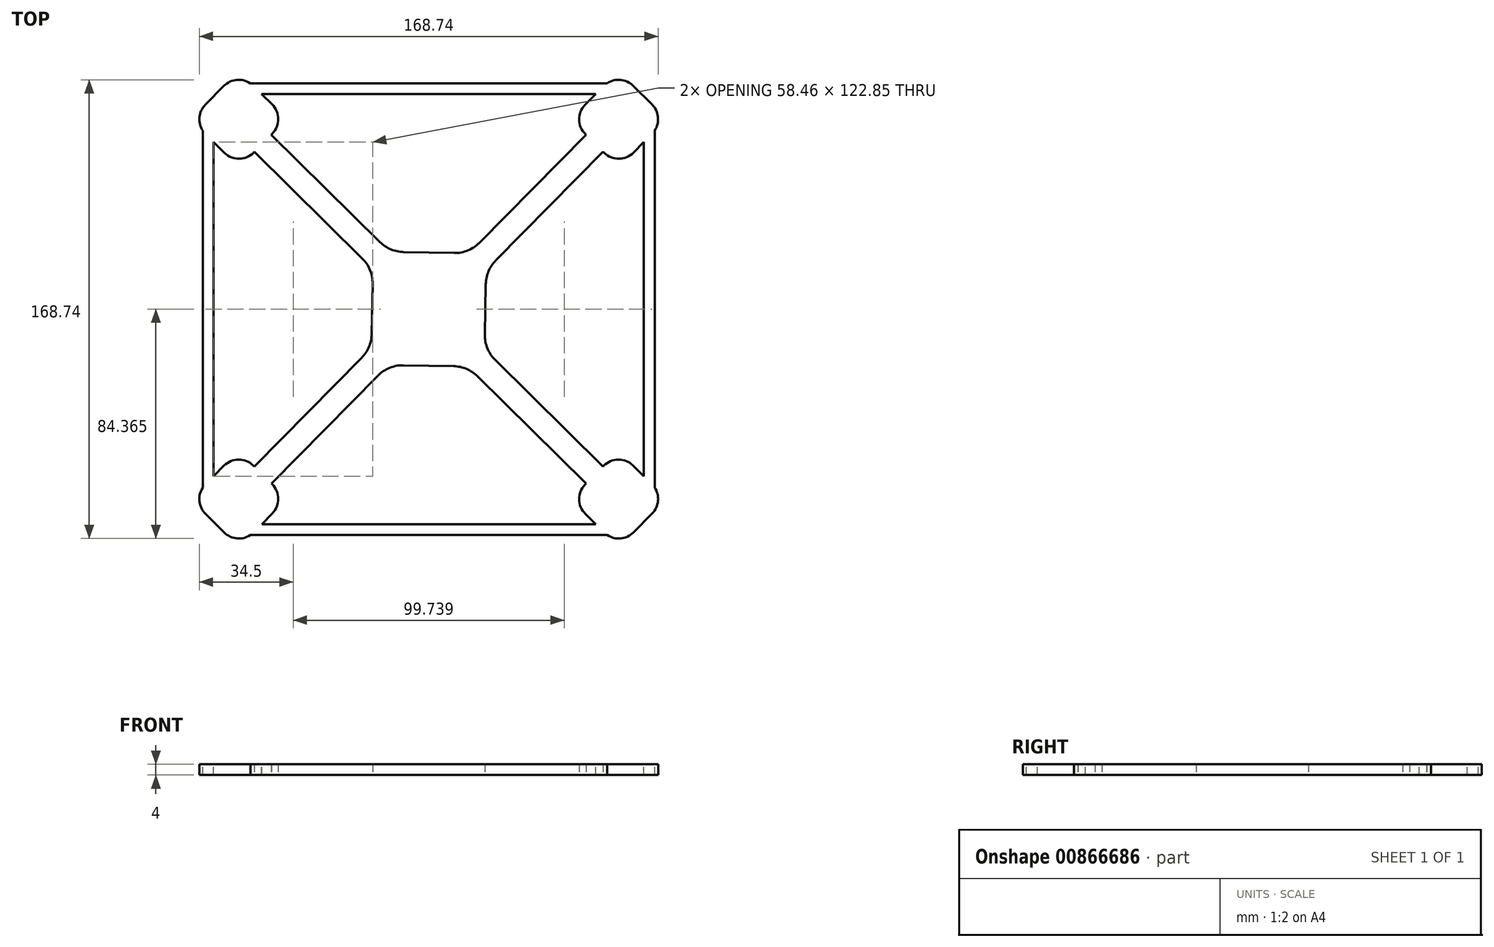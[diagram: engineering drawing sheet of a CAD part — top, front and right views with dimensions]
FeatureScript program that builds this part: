
annotation { "Feature Type Name" : "Feature", "Feature Type Description" : "" }
export const myFeature = defineFeature(function(context is Context, id is Id, definition is map)
    precondition{}
    {
        {
            var Q0;
            Q0=qCreatedBy(makeId("Top.planeOp"),FACE);
            var sketch = newSketch(context, id + "F0", { "sketchPlane" : qUnion([Q0])});
            skCircle(sketch, "E0", {"center": v(-69.85, -69.85) * mm, "radius": 63.5 * mm});
            skCircle(sketch, "E1", {"center": v(69.85, -69.85) * mm, "radius": 63.5 * mm});
            skCircle(sketch, "E2", {"center": v(69.85, 69.85) * mm, "radius": 63.5 * mm});
            skCircle(sketch, "E3", {"center": v(-69.85, 69.85) * mm, "radius": 63.5 * mm});
            skLineSegment(sketch, "E4.0", {"start": v(24.66, 17.89) * mm, "end": v(64.17, 57.89) * mm});
            skLineSegment(sketch, "E5.0", {"start": v(18.6, 24.41) * mm, "end": v(57.85, 64.14) * mm});
            skLineSegment(sketch, "E6", {"start": v(78.63, 78.74) * mm, "end": v(82.1, 75.31) * mm});
            skLineSegment(sketch, "E7", {"start": v(78.63, 78.74) * mm, "end": v(75.16, 82.17) * mm});
            skLineSegment(sketch, "E8", {"start": v(64.39, 82.1) * mm, "end": v(57.53, 75.16) * mm});
            skLineSegment(sketch, "E9", {"start": v(78.74, 61.07) * mm, "end": v(82.17, 64.54) * mm});
            skLineSegment(sketch, "E10", {"start": v(64.17, 57.89) * mm, "end": v(64.54, 57.53) * mm});
            skLineSegment(sketch, "E11", {"start": v(75.31, 57.6) * mm, "end": v(78.74, 61.07) * mm});
            skLineSegment(sketch, "E12", {"start": v(57.6, 64.39) * mm, "end": v(57.85, 64.14) * mm});
            skPoint(sketch, "E13.visualSharp", {"position": v(52.17, 69.74) * mm});
            skPoint(sketch, "E14.visualSharp", {"position": v(69.74, 87.53) * mm});
            skArc(sketch, "E14.filletArc", {"start": v(75.16, 82.17) * mm, "mid": v(69.76, 84.37) * mm, "end": v(64.39, 82.1) * mm});
            skArc(sketch, "E15.filletArc", {"start": v(57.53, 75.16) * mm, "mid": v(55.33, 69.76) * mm, "end": v(57.6, 64.39) * mm});
            skPoint(sketch, "E16.visualSharp", {"position": v(69.96, 52.17) * mm});
            skArc(sketch, "E16.filletArc", {"start": v(64.54, 57.53) * mm, "mid": v(69.94, 55.33) * mm, "end": v(75.31, 57.6) * mm});
            skPoint(sketch, "E17.visualSharp", {"position": v(11.4, 17.11) * mm});
            skLineSegment(sketch, "E18", {"start": v(0, 0) * mm, "end": v(69.85, 69.85) * mm});
            skLineSegment(sketch, "E19", {"start": v(57.85, 64.14) * mm, "end": v(61, 61) * mm});
            skLineSegment(sketch, "E20", {"start": v(61, 61) * mm, "end": v(64.17, 57.89) * mm});
            skPoint(sketch, "E21.1.0", {"position": v(-87.53, 69.74) * mm});
            skLineSegment(sketch, "E21.1.1", {"start": v(-61.07, 78.74) * mm, "end": v(-64.54, 82.17) * mm});
            skPoint(sketch, "E21.1.2", {"position": v(-69.74, 52.17) * mm});
            skPoint(sketch, "E21.1.3", {"position": v(-52.17, 69.96) * mm});
            skLineSegment(sketch, "E21.1.4", {"start": v(-17.89, 24.66) * mm, "end": v(-57.89, 64.17) * mm});
            skLineSegment(sketch, "E21.1.5", {"start": v(-24.41, 18.6) * mm, "end": v(-64.14, 57.85) * mm});
            skLineSegment(sketch, "E21.1.6", {"start": v(0, 0) * mm, "end": v(-69.85, 69.85) * mm});
            skLineSegment(sketch, "E21.1.7", {"start": v(-82.1, 64.39) * mm, "end": v(-75.16, 57.53) * mm});
            skArc(sketch, "E21.1.8", {"start": v(-82.17, 75.16) * mm, "mid": v(-84.37, 69.76) * mm, "end": v(-82.1, 64.39) * mm});
            skPoint(sketch, "E21.1.9", {"position": v(-69.74, 52.17) * mm});
            skArc(sketch, "E21.1.10", {"start": v(-57.53, 64.54) * mm, "mid": v(-55.33, 69.94) * mm, "end": v(-57.6, 75.31) * mm});
            skLineSegment(sketch, "E21.1.11", {"start": v(-78.74, 78.63) * mm, "end": v(-75.31, 82.1) * mm});
            skLineSegment(sketch, "E21.1.12", {"start": v(-78.74, 78.63) * mm, "end": v(-82.17, 75.16) * mm});
            skLineSegment(sketch, "E21.1.13", {"start": v(-57.6, 75.31) * mm, "end": v(-61.07, 78.74) * mm});
            skArc(sketch, "E21.1.14", {"start": v(-75.16, 57.53) * mm, "mid": v(-69.76, 55.33) * mm, "end": v(-64.39, 57.6) * mm});
            skLineSegment(sketch, "E21.1.15", {"start": v(-61, 61) * mm, "end": v(-57.89, 64.17) * mm});
            skLineSegment(sketch, "E21.1.16", {"start": v(-64.14, 57.85) * mm, "end": v(-61, 61) * mm});
            skLineSegment(sketch, "E21.1.17", {"start": v(-57.89, 64.17) * mm, "end": v(-57.53, 64.54) * mm});
            skLineSegment(sketch, "E21.1.18", {"start": v(-64.39, 57.6) * mm, "end": v(-64.14, 57.85) * mm});
            skPoint(sketch, "E21.2.0", {"position": v(-69.74, -87.53) * mm});
            skLineSegment(sketch, "E21.2.1", {"start": v(-78.74, -61.07) * mm, "end": v(-82.17, -64.54) * mm});
            skPoint(sketch, "E21.2.2", {"position": v(-52.17, -69.74) * mm});
            skPoint(sketch, "E21.2.3", {"position": v(-69.96, -52.17) * mm});
            skLineSegment(sketch, "E21.2.4", {"start": v(-24.66, -17.89) * mm, "end": v(-64.17, -57.89) * mm});
            skLineSegment(sketch, "E21.2.5", {"start": v(-18.6, -24.41) * mm, "end": v(-57.85, -64.14) * mm});
            skLineSegment(sketch, "E21.2.6", {"start": v(0, 0) * mm, "end": v(-69.85, -69.85) * mm});
            skLineSegment(sketch, "E21.2.7", {"start": v(-64.39, -82.1) * mm, "end": v(-57.53, -75.16) * mm});
            skArc(sketch, "E21.2.8", {"start": v(-75.16, -82.17) * mm, "mid": v(-69.76, -84.37) * mm, "end": v(-64.39, -82.1) * mm});
            skPoint(sketch, "E21.2.9", {"position": v(-52.17, -69.74) * mm});
            skArc(sketch, "E21.2.10", {"start": v(-64.54, -57.53) * mm, "mid": v(-69.94, -55.33) * mm, "end": v(-75.31, -57.6) * mm});
            skLineSegment(sketch, "E21.2.11", {"start": v(-78.63, -78.74) * mm, "end": v(-82.1, -75.31) * mm});
            skLineSegment(sketch, "E21.2.12", {"start": v(-78.63, -78.74) * mm, "end": v(-75.16, -82.17) * mm});
            skLineSegment(sketch, "E21.2.13", {"start": v(-75.31, -57.6) * mm, "end": v(-78.74, -61.07) * mm});
            skArc(sketch, "E21.2.14", {"start": v(-57.53, -75.16) * mm, "mid": v(-55.33, -69.76) * mm, "end": v(-57.6, -64.39) * mm});
            skLineSegment(sketch, "E21.2.15", {"start": v(-61, -61) * mm, "end": v(-64.17, -57.89) * mm});
            skLineSegment(sketch, "E21.2.16", {"start": v(-57.85, -64.14) * mm, "end": v(-61, -61) * mm});
            skLineSegment(sketch, "E21.2.17", {"start": v(-64.17, -57.89) * mm, "end": v(-64.54, -57.53) * mm});
            skLineSegment(sketch, "E21.2.18", {"start": v(-57.6, -64.39) * mm, "end": v(-57.85, -64.14) * mm});
            skPoint(sketch, "E21.3.0", {"position": v(87.53, -69.74) * mm});
            skLineSegment(sketch, "E21.3.1", {"start": v(61.07, -78.74) * mm, "end": v(64.54, -82.17) * mm});
            skPoint(sketch, "E21.3.2", {"position": v(69.74, -52.17) * mm});
            skPoint(sketch, "E21.3.3", {"position": v(52.17, -69.96) * mm});
            skLineSegment(sketch, "E21.3.4", {"start": v(17.89, -24.66) * mm, "end": v(57.89, -64.17) * mm});
            skLineSegment(sketch, "E21.3.5", {"start": v(24.41, -18.6) * mm, "end": v(64.14, -57.85) * mm});
            skLineSegment(sketch, "E21.3.6", {"start": v(0, 0) * mm, "end": v(69.85, -69.85) * mm});
            skLineSegment(sketch, "E21.3.7", {"start": v(82.1, -64.39) * mm, "end": v(75.16, -57.53) * mm});
            skArc(sketch, "E21.3.8", {"start": v(82.17, -75.16) * mm, "mid": v(84.37, -69.76) * mm, "end": v(82.1, -64.39) * mm});
            skPoint(sketch, "E21.3.9", {"position": v(69.74, -52.17) * mm});
            skArc(sketch, "E21.3.10", {"start": v(57.53, -64.54) * mm, "mid": v(55.33, -69.94) * mm, "end": v(57.6, -75.31) * mm});
            skLineSegment(sketch, "E21.3.11", {"start": v(78.74, -78.63) * mm, "end": v(75.31, -82.1) * mm});
            skLineSegment(sketch, "E21.3.12", {"start": v(78.74, -78.63) * mm, "end": v(82.17, -75.16) * mm});
            skLineSegment(sketch, "E21.3.13", {"start": v(57.6, -75.31) * mm, "end": v(61.07, -78.74) * mm});
            skArc(sketch, "E21.3.14", {"start": v(75.16, -57.53) * mm, "mid": v(69.76, -55.33) * mm, "end": v(64.39, -57.6) * mm});
            skLineSegment(sketch, "E21.3.15", {"start": v(61, -61) * mm, "end": v(57.89, -64.17) * mm});
            skLineSegment(sketch, "E21.3.16", {"start": v(64.14, -57.85) * mm, "end": v(61, -61) * mm});
            skLineSegment(sketch, "E21.3.17", {"start": v(57.89, -64.17) * mm, "end": v(57.53, -64.54) * mm});
            skLineSegment(sketch, "E21.3.18", {"start": v(64.39, -57.6) * mm, "end": v(64.14, -57.85) * mm});
            skPoint(sketch, "E21.center", {"position": v(0, 0) * mm});
            skLineSegment(sketch, "E22", {"start": v(21, 9.2) * mm, "end": v(20.64, -9.33) * mm});
            skLineSegment(sketch, "E23", {"start": v(9.2, -21) * mm, "end": v(-9.33, -20.64) * mm});
            skLineSegment(sketch, "E24", {"start": v(-21, -9.2) * mm, "end": v(-20.64, 9.33) * mm});
            skLineSegment(sketch, "E25", {"start": v(-9.2, 21) * mm, "end": v(9.33, 20.64) * mm});
            skPoint(sketch, "E26.visualSharp", {"position": v(69.96, -87.53) * mm});
            skArc(sketch, "E26.filletArc", {"start": v(64.54, -82.17) * mm, "mid": v(69.94, -84.37) * mm, "end": v(75.31, -82.1) * mm});
            skPoint(sketch, "E27.visualSharp", {"position": v(-87.53, -69.96) * mm});
            skArc(sketch, "E27.filletArc", {"start": v(-82.17, -64.54) * mm, "mid": v(-84.37, -69.94) * mm, "end": v(-82.1, -75.31) * mm});
            skPoint(sketch, "E28.visualSharp", {"position": v(-69.96, 87.53) * mm});
            skArc(sketch, "E28.filletArc", {"start": v(-64.54, 82.17) * mm, "mid": v(-69.94, 84.37) * mm, "end": v(-75.31, 82.1) * mm});
            skPoint(sketch, "E29.visualSharp", {"position": v(87.53, 69.96) * mm});
            skArc(sketch, "E29.filletArc", {"start": v(82.17, 64.54) * mm, "mid": v(84.37, 69.94) * mm, "end": v(82.1, 75.31) * mm});
            skPoint(sketch, "E30.visualSharp", {"position": v(-14.28, 21.1) * mm});
            skArc(sketch, "E30.filletArc", {"start": v(-17.89, 24.66) * mm, "mid": v(-13.9, 21.99) * mm, "end": v(-9.2, 21) * mm});
            skPoint(sketch, "E31.visualSharp", {"position": v(-20.53, 14.77) * mm});
            skArc(sketch, "E31.filletArc", {"start": v(-20.64, 9.33) * mm, "mid": v(-21.57, 14.35) * mm, "end": v(-24.41, 18.6) * mm});
            skPoint(sketch, "E32.visualSharp", {"position": v(-21.1, -14.28) * mm});
            skArc(sketch, "E32.filletArc", {"start": v(-24.66, -17.89) * mm, "mid": v(-21.99, -13.9) * mm, "end": v(-21, -9.2) * mm});
            skPoint(sketch, "E33.visualSharp", {"position": v(-14.77, -20.53) * mm});
            skArc(sketch, "E33.filletArc", {"start": v(-9.33, -20.64) * mm, "mid": v(-14.35, -21.57) * mm, "end": v(-18.6, -24.41) * mm});
            skPoint(sketch, "E34.visualSharp", {"position": v(14.28, -21.1) * mm});
            skArc(sketch, "E34.filletArc", {"start": v(17.89, -24.66) * mm, "mid": v(13.9, -21.99) * mm, "end": v(9.2, -21) * mm});
            skPoint(sketch, "E35.visualSharp", {"position": v(20.53, -14.77) * mm});
            skArc(sketch, "E35.filletArc", {"start": v(20.64, -9.33) * mm, "mid": v(21.57, -14.35) * mm, "end": v(24.41, -18.6) * mm});
            skPoint(sketch, "E36.visualSharp", {"position": v(21.1, 14.28) * mm});
            skArc(sketch, "E36.filletArc", {"start": v(24.66, 17.89) * mm, "mid": v(21.99, 13.9) * mm, "end": v(21, 9.2) * mm});
            skPoint(sketch, "E37.visualSharp", {"position": v(14.77, 20.53) * mm});
            skArc(sketch, "E37.filletArc", {"start": v(9.33, 20.64) * mm, "mid": v(14.35, 21.57) * mm, "end": v(18.6, 24.41) * mm});
            skSolve(sketch);
        }
        {
            var Q0;
            Q0=makeQuery(id+"F0.imprint","IMPRINT",FACE,{"disambiguationData":[TD([[makeQuery(id+"F0.imprint","IMPRINT",EDGE,{"derivedFrom":sQuery(id+"F0.wireOp",EDGE,"E21.1.1")}),1.0]])]});
            var Q1;
            {var subQ5=sQuery(id+"F0.wireOp",EDGE,"E21.1.15");Q1=makeQuery(id+"F0.imprint","IMPRINT",FACE,{"disambiguationData":[TD([[makeQuery(id+"F0.imprint","IMPRINT",EDGE,{"derivedFrom":subQ5}),-1.0]])]});}
            var Q2;
            {var subQ5=sQuery(id+"F0.wireOp",EDGE,"E21.1.16");Q2=makeQuery(id+"F0.imprint","IMPRINT",FACE,{"disambiguationData":[TD([[makeQuery(id+"F0.imprint","IMPRINT",EDGE,{"derivedFrom":subQ5}),-1.0]])]});}
            var Q3;
            Q3=makeQuery(id+"F0.imprint","IMPRINT",FACE,{"disambiguationData":[TD([[makeQuery(id+"F0.imprint","IMPRINT",EDGE,{"derivedFrom":sQuery(id+"F0.wireOp",EDGE,"E25")}),-1.0]])]});
            var Q4;
            Q4=makeQuery(id+"F0.imprint","IMPRINT",FACE,{"disambiguationData":[TD([[makeQuery(id+"F0.imprint","IMPRINT",EDGE,{"derivedFrom":sQuery(id+"F0.wireOp",EDGE,"E24")}),-1.0]])]});
            var Q5;
            Q5=makeQuery(id+"F0.imprint","IMPRINT",FACE,{"disambiguationData":[TD([[makeQuery(id+"F0.imprint","IMPRINT",EDGE,{"derivedFrom":sQuery(id+"F0.wireOp",EDGE,"E23")}),-1.0]])]});
            var Q6;
            Q6=makeQuery(id+"F0.imprint","IMPRINT",FACE,{"disambiguationData":[TD([[makeQuery(id+"F0.imprint","IMPRINT",EDGE,{"derivedFrom":sQuery(id+"F0.wireOp",EDGE,"E22")}),-1.0]])]});
            var Q7;
            {var subQ5=sQuery(id+"F0.wireOp",EDGE,"E20");Q7=makeQuery(id+"F0.imprint","IMPRINT",FACE,{"disambiguationData":[TD([[makeQuery(id+"F0.imprint","IMPRINT",EDGE,{"derivedFrom":subQ5}),-1.0]])]});}
            var Q8;
            {var subQ5=sQuery(id+"F0.wireOp",EDGE,"E19");Q8=makeQuery(id+"F0.imprint","IMPRINT",FACE,{"disambiguationData":[TD([[makeQuery(id+"F0.imprint","IMPRINT",EDGE,{"derivedFrom":subQ5}),-1.0]])]});}
            var Q9;
            Q9=makeQuery(id+"F0.imprint","IMPRINT",FACE,{"disambiguationData":[TD([[makeQuery(id+"F0.imprint","IMPRINT",EDGE,{"derivedFrom":sQuery(id+"F0.wireOp",EDGE,"E6")}),-1.0]])]});
            var Q10;
            Q10=makeQuery(id+"F0.imprint","IMPRINT",FACE,{"disambiguationData":[TD([[makeQuery(id+"F0.imprint","IMPRINT",EDGE,{"derivedFrom":sQuery(id+"F0.wireOp",EDGE,"E21.3.1")}),1.0]])]});
            var Q11;
            {var subQ5=sQuery(id+"F0.wireOp",EDGE,"E21.3.16");Q11=makeQuery(id+"F0.imprint","IMPRINT",FACE,{"disambiguationData":[TD([[makeQuery(id+"F0.imprint","IMPRINT",EDGE,{"derivedFrom":subQ5}),-1.0]])]});}
            var Q12;
            {var subQ5=sQuery(id+"F0.wireOp",EDGE,"E21.3.15");Q12=makeQuery(id+"F0.imprint","IMPRINT",FACE,{"disambiguationData":[TD([[makeQuery(id+"F0.imprint","IMPRINT",EDGE,{"derivedFrom":subQ5}),-1.0]])]});}
            var Q13;
            {var subQ5=sQuery(id+"F0.wireOp",EDGE,"E21.2.16");Q13=makeQuery(id+"F0.imprint","IMPRINT",FACE,{"disambiguationData":[TD([[makeQuery(id+"F0.imprint","IMPRINT",EDGE,{"derivedFrom":subQ5}),-1.0]])]});}
            var Q14;
            {var subQ5=sQuery(id+"F0.wireOp",EDGE,"E21.2.15");Q14=makeQuery(id+"F0.imprint","IMPRINT",FACE,{"disambiguationData":[TD([[makeQuery(id+"F0.imprint","IMPRINT",EDGE,{"derivedFrom":subQ5}),-1.0]])]});}
            var Q15;
            Q15=makeQuery(id+"F0.imprint","IMPRINT",FACE,{"disambiguationData":[TD([[makeQuery(id+"F0.imprint","IMPRINT",EDGE,{"derivedFrom":sQuery(id+"F0.wireOp",EDGE,"E21.2.1")}),1.0]])]});
            extrude(context, id + "F1", {"entities" : qUnion([Q0, Q1, Q2, Q3, Q4, Q5, Q6, Q7, Q8, Q9, Q10, Q11, Q12, Q13, Q14, Q15]), "depth" : 4 * mm, "offsetDistance" : 25.4 * mm});
        }
        {
            var Q0;
            Q0=makeQuery(id+"F1.opExtrude","CAP_FACE",FACE,{"disambiguationData":[OSD([sQuery(id+"F0.wireOp",EDGE,"E4.0"),sQuery(id+"F0.wireOp",EDGE,"E5.0"),sQuery(id+"F0.wireOp",EDGE,"E6"),sQuery(id+"F0.wireOp",EDGE,"E7"),sQuery(id+"F0.wireOp",EDGE,"E8"),sQuery(id+"F0.wireOp",EDGE,"E9"),sQuery(id+"F0.wireOp",EDGE,"E10"),sQuery(id+"F0.wireOp",EDGE,"E11"),sQuery(id+"F0.wireOp",EDGE,"E12"),sQuery(id+"F0.wireOp",EDGE,"E14.filletArc"),sQuery(id+"F0.wireOp",EDGE,"E15.filletArc"),sQuery(id+"F0.wireOp",EDGE,"E16.filletArc"),sQuery(id+"F0.wireOp",EDGE,"E21.1.1"),sQuery(id+"F0.wireOp",EDGE,"E21.1.4"),sQuery(id+"F0.wireOp",EDGE,"E21.1.5"),sQuery(id+"F0.wireOp",EDGE,"E21.1.7"),sQuery(id+"F0.wireOp",EDGE,"E21.1.8"),sQuery(id+"F0.wireOp",EDGE,"E21.1.10"),sQuery(id+"F0.wireOp",EDGE,"E21.1.11"),sQuery(id+"F0.wireOp",EDGE,"E21.1.12"),sQuery(id+"F0.wireOp",EDGE,"E21.1.13"),sQuery(id+"F0.wireOp",EDGE,"E21.1.14"),sQuery(id+"F0.wireOp",EDGE,"E21.1.17"),sQuery(id+"F0.wireOp",EDGE,"E21.1.18"),sQuery(id+"F0.wireOp",EDGE,"E21.2.1"),sQuery(id+"F0.wireOp",EDGE,"E21.2.4"),sQuery(id+"F0.wireOp",EDGE,"E21.2.5"),sQuery(id+"F0.wireOp",EDGE,"E21.2.7"),sQuery(id+"F0.wireOp",EDGE,"E21.2.8"),sQuery(id+"F0.wireOp",EDGE,"E21.2.10"),sQuery(id+"F0.wireOp",EDGE,"E21.2.11"),sQuery(id+"F0.wireOp",EDGE,"E21.2.12"),sQuery(id+"F0.wireOp",EDGE,"E21.2.13"),sQuery(id+"F0.wireOp",EDGE,"E21.2.14"),sQuery(id+"F0.wireOp",EDGE,"E21.2.17"),sQuery(id+"F0.wireOp",EDGE,"E21.2.18"),sQuery(id+"F0.wireOp",EDGE,"E21.3.1"),sQuery(id+"F0.wireOp",EDGE,"E21.3.4"),sQuery(id+"F0.wireOp",EDGE,"E21.3.5"),sQuery(id+"F0.wireOp",EDGE,"E21.3.7"),sQuery(id+"F0.wireOp",EDGE,"E21.3.8"),sQuery(id+"F0.wireOp",EDGE,"E21.3.10"),sQuery(id+"F0.wireOp",EDGE,"E21.3.11"),sQuery(id+"F0.wireOp",EDGE,"E21.3.12"),sQuery(id+"F0.wireOp",EDGE,"E21.3.13"),sQuery(id+"F0.wireOp",EDGE,"E21.3.14"),sQuery(id+"F0.wireOp",EDGE,"E21.3.17"),sQuery(id+"F0.wireOp",EDGE,"E21.3.18"),sQuery(id+"F0.wireOp",EDGE,"E22"),sQuery(id+"F0.wireOp",EDGE,"E23"),sQuery(id+"F0.wireOp",EDGE,"E24"),sQuery(id+"F0.wireOp",EDGE,"E25"),sQuery(id+"F0.wireOp",EDGE,"E26.filletArc"),sQuery(id+"F0.wireOp",EDGE,"E27.filletArc"),sQuery(id+"F0.wireOp",EDGE,"E28.filletArc"),sQuery(id+"F0.wireOp",EDGE,"E29.filletArc"),sQuery(id+"F0.wireOp",EDGE,"E30.filletArc"),sQuery(id+"F0.wireOp",EDGE,"E31.filletArc"),sQuery(id+"F0.wireOp",EDGE,"E32.filletArc"),sQuery(id+"F0.wireOp",EDGE,"E33.filletArc"),sQuery(id+"F0.wireOp",EDGE,"E34.filletArc"),sQuery(id+"F0.wireOp",EDGE,"E35.filletArc"),sQuery(id+"F0.wireOp",EDGE,"E36.filletArc"),sQuery(id+"F0.wireOp",EDGE,"E37.filletArc")])],"isStart":false});
            var sketch = newSketch(context, id + "F2", { "sketchPlane" : qUnion([Q0])});
            skLineSegment(sketch, "E38", {"start": v(-69.85, -83.1) * mm, "end": v(69.85, -83.1) * mm});
            skPoint(sketch, "E38.startSnap0", {"position": v(-69.77, -83.1) * mm});
            skLineSegment(sketch, "E39.0", {"start": v(-63.2, -79.1) * mm, "end": v(63.24, -79.1) * mm});
            skLineSegment(sketch, "E40.1.0", {"start": v(83.1, -69.85) * mm, "end": v(83.1, 69.85) * mm});
            skLineSegment(sketch, "E40.1.1", {"start": v(79.1, -63.2) * mm, "end": v(79.1, 63.24) * mm});
            skLineSegment(sketch, "E40.2.0", {"start": v(69.85, 83.1) * mm, "end": v(-69.85, 83.1) * mm});
            skLineSegment(sketch, "E40.2.1", {"start": v(63.2, 79.1) * mm, "end": v(-63.24, 79.1) * mm});
            skLineSegment(sketch, "E40.3.0", {"start": v(-83.1, 69.85) * mm, "end": v(-83.1, -69.85) * mm});
            skLineSegment(sketch, "E40.3.1", {"start": v(-79.1, 63.2) * mm, "end": v(-79.1, -63.24) * mm});
            skPoint(sketch, "E40.center", {"position": v(0, 0) * mm});
            skSolve(sketch);
        }
        {
            var Q0;
            {var subQ11=sQuery(id+"F2.wireOp",EDGE,"E40.2.1");Q0=makeQuery(id+"F2.imprint","IMPRINT",FACE,{"disambiguationData":[TD([[makeQuery(id+"F2.imprint","IMPRINT",EDGE,{"derivedFrom":subQ11}),-1.0]])]});}
            var Q1;
            {var subQ9=sQuery(id+"F2.wireOp",EDGE,"E40.3.1");Q1=makeQuery(id+"F2.imprint","IMPRINT",FACE,{"disambiguationData":[TD([[makeQuery(id+"F2.imprint","IMPRINT",EDGE,{"derivedFrom":subQ9}),-1.0]])]});}
            var Q2;
            {var subQ9=sQuery(id+"F2.wireOp",EDGE,"E39.0");Q2=makeQuery(id+"F2.imprint","IMPRINT",FACE,{"disambiguationData":[TD([[makeQuery(id+"F2.imprint","IMPRINT",EDGE,{"derivedFrom":subQ9}),-1.0]])]});}
            var Q3;
            {var subQ9=sQuery(id+"F2.wireOp",EDGE,"E40.1.1");Q3=makeQuery(id+"F2.imprint","IMPRINT",FACE,{"disambiguationData":[TD([[makeQuery(id+"F2.imprint","IMPRINT",EDGE,{"derivedFrom":subQ9}),-1.0]])]});}
            extrude(context, id + "F3", {"entities" : qUnion([Q0, Q1, Q2, Q3]), "operationType" : NewBodyOperationType.ADD, "depth" : -4 * mm, "offsetDistance" : 25.4 * mm});
        }
    });
